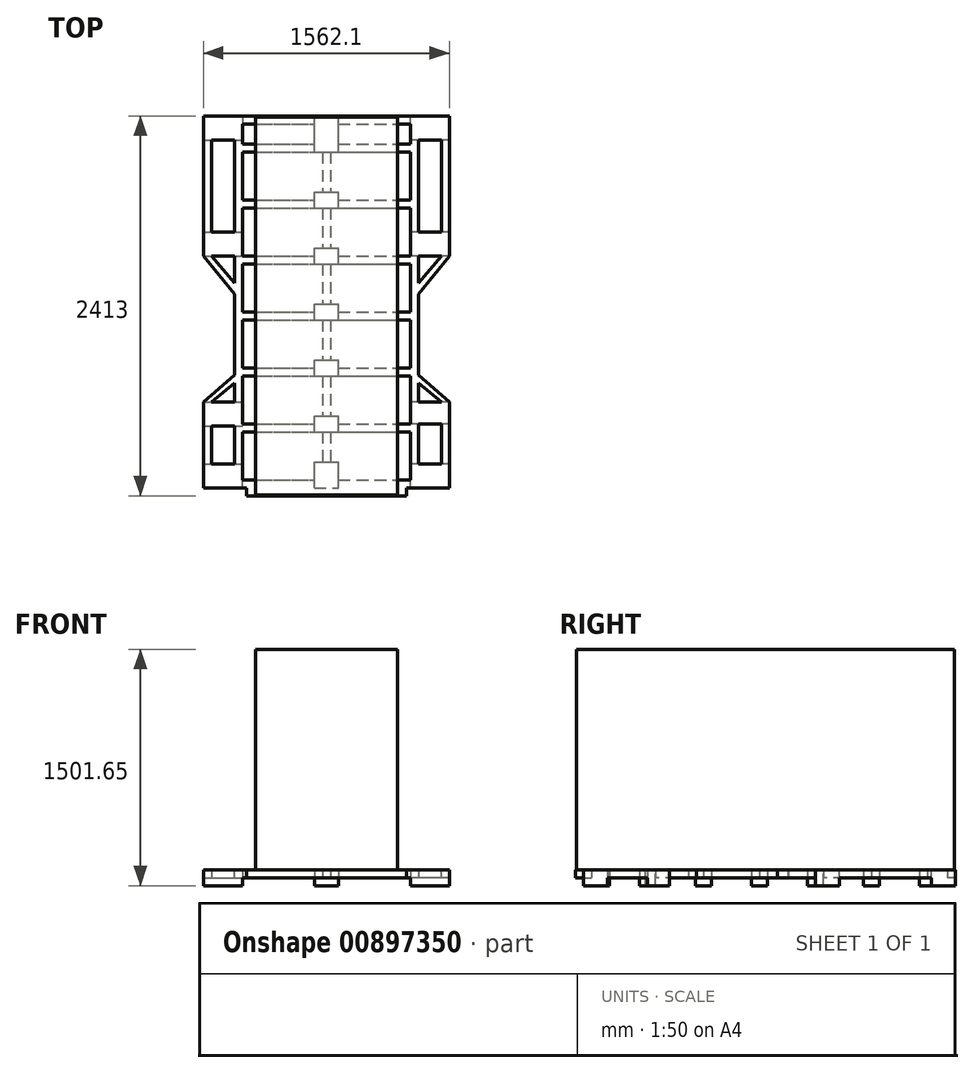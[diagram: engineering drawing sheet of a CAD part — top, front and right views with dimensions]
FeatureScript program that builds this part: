
annotation { "Feature Type Name" : "Feature", "Feature Type Description" : "" }
export const myFeature = defineFeature(function(context is Context, id is Id, definition is map)
    precondition{}
    {
        {
            var Q0;
            Q0=qCreatedBy(makeId("Top.planeOp"),FACE);
            var sketch = newSketch(context, id + "F0", { "sketchPlane" : qUnion([Q0])});
            skLineSegment(sketch, "E0.bottom", {"start": v(-826.89, 249) * mm, "end": v(341.51, 249) * mm});
            skLineSegment(sketch, "E0.top", {"start": v(-826.89, 299.8) * mm, "end": v(341.51, 299.8) * mm});
            skLineSegment(sketch, "E0.left", {"start": v(-826.89, 249) * mm, "end": v(-826.89, 299.8) * mm});
            skLineSegment(sketch, "E0.right", {"start": v(341.51, 249) * mm, "end": v(341.51, 299.8) * mm});
            skLineSegment(sketch, "E1.bottom", {"start": v(341.51, 299.8) * mm, "end": v(290.71, 299.8) * mm});
            skLineSegment(sketch, "E1.top", {"start": v(341.51, 2611.2) * mm, "end": v(290.71, 2611.2) * mm});
            skLineSegment(sketch, "E1.left", {"start": v(341.51, 299.8) * mm, "end": v(341.51, 2611.2) * mm});
            skLineSegment(sketch, "E1.right", {"start": v(290.71, 299.8) * mm, "end": v(290.71, 2611.2) * mm});
            skLineSegment(sketch, "E2.bottom", {"start": v(-826.89, 299.8) * mm, "end": v(-776.09, 299.8) * mm});
            skLineSegment(sketch, "E2.top", {"start": v(-826.89, 2611.2) * mm, "end": v(-776.09, 2611.2) * mm});
            skLineSegment(sketch, "E2.left", {"start": v(-826.89, 299.8) * mm, "end": v(-826.89, 2611.2) * mm});
            skLineSegment(sketch, "E2.right", {"start": v(-776.09, 299.8) * mm, "end": v(-776.09, 2611.2) * mm});
            skLineSegment(sketch, "E3.bottom", {"start": v(-826.89, 2611.2) * mm, "end": v(341.51, 2611.2) * mm});
            skLineSegment(sketch, "E3.top", {"start": v(-826.89, 2560.4) * mm, "end": v(341.51, 2560.4) * mm});
            skLineSegment(sketch, "E3.left", {"start": v(-826.89, 2611.2) * mm, "end": v(-826.89, 2560.4) * mm});
            skLineSegment(sketch, "E3.right", {"start": v(341.51, 2611.2) * mm, "end": v(341.51, 2560.4) * mm});
            skLineSegment(sketch, "E4.bottom", {"start": v(-826.89, 2611.2) * mm, "end": v(-1023.74, 2611.2) * mm});
            skLineSegment(sketch, "E4.top", {"start": v(-826.89, 2560.4) * mm, "end": v(-1023.74, 2560.4) * mm});
            skLineSegment(sketch, "E4.right", {"start": v(-1023.74, 2611.2) * mm, "end": v(-1023.74, 2560.4) * mm});
            skLineSegment(sketch, "E5.bottom", {"start": v(341.51, 2611.2) * mm, "end": v(538.36, 2611.2) * mm});
            skLineSegment(sketch, "E5.top", {"start": v(341.51, 2560.4) * mm, "end": v(538.36, 2560.4) * mm});
            skLineSegment(sketch, "E5.right", {"start": v(538.36, 2611.2) * mm, "end": v(538.36, 2560.4) * mm});
            skLineSegment(sketch, "E6.bottom", {"start": v(-1023.74, 2560.4) * mm, "end": v(-972.94, 2560.4) * mm});
            skLineSegment(sketch, "E6.top", {"start": v(-1023.74, 1722.2) * mm, "end": v(-972.94, 1722.2) * mm});
            skLineSegment(sketch, "E6.left", {"start": v(-1023.74, 2560.4) * mm, "end": v(-1023.74, 1722.2) * mm});
            skLineSegment(sketch, "E6.right", {"start": v(-972.94, 2560.4) * mm, "end": v(-972.94, 1722.2) * mm});
            skLineSegment(sketch, "E7.bottom", {"start": v(538.36, 2560.4) * mm, "end": v(487.56, 2560.4) * mm});
            skLineSegment(sketch, "E7.top", {"start": v(538.36, 1722.2) * mm, "end": v(487.56, 1722.2) * mm});
            skLineSegment(sketch, "E7.left", {"start": v(538.36, 2560.4) * mm, "end": v(538.36, 1722.2) * mm});
            skLineSegment(sketch, "E7.right", {"start": v(487.56, 2560.4) * mm, "end": v(487.56, 1722.2) * mm});
            skLineSegment(sketch, "E8", {"start": v(341.51, 2560.4) * mm, "end": v(341.51, 1480.9) * mm});
            skLineSegment(sketch, "E9", {"start": v(-826.89, 2560.4) * mm, "end": v(-826.89, 1480.9) * mm});
            skLineSegment(sketch, "E10", {"start": v(341.51, 1480.9) * mm, "end": v(538.36, 1722.2) * mm});
            skLineSegment(sketch, "E11", {"start": v(-1023.74, 1722.2) * mm, "end": v(-826.89, 1480.9) * mm});
            skLineSegment(sketch, "E12.bottom", {"start": v(341.51, 249) * mm, "end": v(538.36, 249) * mm});
            skLineSegment(sketch, "E12.top", {"start": v(341.51, 299.8) * mm, "end": v(538.36, 299.8) * mm});
            skLineSegment(sketch, "E12.right", {"start": v(538.36, 249) * mm, "end": v(538.36, 299.8) * mm});
            skLineSegment(sketch, "E13.bottom", {"start": v(-826.89, 249) * mm, "end": v(-1023.74, 249) * mm});
            skLineSegment(sketch, "E13.top", {"start": v(-826.89, 299.8) * mm, "end": v(-1023.74, 299.8) * mm});
            skLineSegment(sketch, "E13.right", {"start": v(-1023.74, 249) * mm, "end": v(-1023.74, 299.8) * mm});
            skLineSegment(sketch, "E14.bottom", {"start": v(-1023.74, 299.8) * mm, "end": v(-972.94, 299.8) * mm});
            skLineSegment(sketch, "E14.top", {"start": v(-1023.74, 795.1) * mm, "end": v(-972.94, 795.1) * mm});
            skLineSegment(sketch, "E14.left", {"start": v(-1023.74, 299.8) * mm, "end": v(-1023.74, 795.1) * mm});
            skLineSegment(sketch, "E14.right", {"start": v(-972.94, 299.8) * mm, "end": v(-972.94, 795.1) * mm});
            skLineSegment(sketch, "E15.bottom", {"start": v(538.36, 299.8) * mm, "end": v(487.56, 299.8) * mm});
            skLineSegment(sketch, "E15.top", {"start": v(538.36, 795.1) * mm, "end": v(487.56, 795.1) * mm});
            skLineSegment(sketch, "E15.left", {"start": v(538.36, 299.8) * mm, "end": v(538.36, 795.1) * mm});
            skLineSegment(sketch, "E15.right", {"start": v(487.56, 299.8) * mm, "end": v(487.56, 795.1) * mm});
            skLineSegment(sketch, "E16", {"start": v(-1023.74, 795.1) * mm, "end": v(-826.89, 966.54) * mm});
            skLineSegment(sketch, "E17", {"start": v(538.36, 795.1) * mm, "end": v(341.51, 966.54) * mm});
            skLineSegment(sketch, "E18.bottom", {"start": v(-776.09, 604.6) * mm, "end": v(290.71, 604.6) * mm});
            skLineSegment(sketch, "E18.top", {"start": v(-776.09, 655.4) * mm, "end": v(290.71, 655.4) * mm});
            skLineSegment(sketch, "E18.left", {"start": v(-776.09, 604.6) * mm, "end": v(-776.09, 655.4) * mm});
            skLineSegment(sketch, "E18.right", {"start": v(290.71, 604.6) * mm, "end": v(290.71, 655.4) * mm});
            skLineSegment(sketch, "E19.bottom", {"start": v(-776.09, 1011) * mm, "end": v(290.71, 1011) * mm});
            skLineSegment(sketch, "E19.top", {"start": v(-776.09, 960.2) * mm, "end": v(290.71, 960.2) * mm});
            skLineSegment(sketch, "E19.left", {"start": v(-776.09, 1011) * mm, "end": v(-776.09, 960.2) * mm});
            skLineSegment(sketch, "E19.right", {"start": v(290.71, 1011) * mm, "end": v(290.71, 960.2) * mm});
            skLineSegment(sketch, "E20.bottom", {"start": v(-776.09, 1366.6) * mm, "end": v(290.71, 1366.6) * mm});
            skLineSegment(sketch, "E20.top", {"start": v(-776.09, 1315.8) * mm, "end": v(290.71, 1315.8) * mm});
            skLineSegment(sketch, "E20.left", {"start": v(-776.09, 1366.6) * mm, "end": v(-776.09, 1315.8) * mm});
            skLineSegment(sketch, "E20.right", {"start": v(290.71, 1366.6) * mm, "end": v(290.71, 1315.8) * mm});
            skLineSegment(sketch, "E21.bottom", {"start": v(-776.09, 1722.2) * mm, "end": v(290.71, 1722.2) * mm});
            skLineSegment(sketch, "E21.top", {"start": v(-776.09, 1671.4) * mm, "end": v(290.71, 1671.4) * mm});
            skLineSegment(sketch, "E21.left", {"start": v(-776.09, 1722.2) * mm, "end": v(-776.09, 1671.4) * mm});
            skLineSegment(sketch, "E21.right", {"start": v(290.71, 1722.2) * mm, "end": v(290.71, 1671.4) * mm});
            skLineSegment(sketch, "E22.bottom", {"start": v(-776.09, 2077.8) * mm, "end": v(290.71, 2077.8) * mm});
            skLineSegment(sketch, "E22.top", {"start": v(-776.09, 2027) * mm, "end": v(290.71, 2027) * mm});
            skLineSegment(sketch, "E22.left", {"start": v(-776.09, 2077.8) * mm, "end": v(-776.09, 2027) * mm});
            skLineSegment(sketch, "E22.right", {"start": v(290.71, 2077.8) * mm, "end": v(290.71, 2027) * mm});
            skLineSegment(sketch, "E23.bottom", {"start": v(-776.09, 2433.4) * mm, "end": v(290.71, 2433.4) * mm});
            skLineSegment(sketch, "E23.top", {"start": v(-776.09, 2382.6) * mm, "end": v(290.71, 2382.6) * mm});
            skLineSegment(sketch, "E23.left", {"start": v(-776.09, 2433.4) * mm, "end": v(-776.09, 2382.6) * mm});
            skLineSegment(sketch, "E23.right", {"start": v(290.71, 2433.4) * mm, "end": v(290.71, 2382.6) * mm});
            skLineSegment(sketch, "E24.bottom", {"start": v(-268.09, 2560.4) * mm, "end": v(-217.29, 2560.4) * mm});
            skLineSegment(sketch, "E24.top", {"start": v(-268.09, 2433.4) * mm, "end": v(-217.29, 2433.4) * mm});
            skLineSegment(sketch, "E24.left", {"start": v(-268.09, 2560.4) * mm, "end": v(-268.09, 2433.4) * mm});
            skLineSegment(sketch, "E24.right", {"start": v(-217.29, 2560.4) * mm, "end": v(-217.29, 2433.4) * mm});
            skLineSegment(sketch, "E25.bottom", {"start": v(-268.09, 2382.6) * mm, "end": v(-217.29, 2382.6) * mm});
            skLineSegment(sketch, "E25.top", {"start": v(-268.09, 2077.8) * mm, "end": v(-217.29, 2077.8) * mm});
            skLineSegment(sketch, "E25.left", {"start": v(-268.09, 2382.6) * mm, "end": v(-268.09, 2077.8) * mm});
            skLineSegment(sketch, "E25.right", {"start": v(-217.29, 2382.6) * mm, "end": v(-217.29, 2077.8) * mm});
            skLineSegment(sketch, "E26.bottom", {"start": v(-268.09, 2027) * mm, "end": v(-217.29, 2027) * mm});
            skLineSegment(sketch, "E26.top", {"start": v(-268.09, 1722.2) * mm, "end": v(-217.29, 1722.2) * mm});
            skLineSegment(sketch, "E26.left", {"start": v(-268.09, 2027) * mm, "end": v(-268.09, 1722.2) * mm});
            skLineSegment(sketch, "E26.right", {"start": v(-217.29, 2027) * mm, "end": v(-217.29, 1722.2) * mm});
            skLineSegment(sketch, "E27.bottom", {"start": v(-268.09, 1671.4) * mm, "end": v(-217.29, 1671.4) * mm});
            skLineSegment(sketch, "E27.top", {"start": v(-268.09, 1366.6) * mm, "end": v(-217.29, 1366.6) * mm});
            skLineSegment(sketch, "E27.left", {"start": v(-268.09, 1671.4) * mm, "end": v(-268.09, 1366.6) * mm});
            skLineSegment(sketch, "E27.right", {"start": v(-217.29, 1671.4) * mm, "end": v(-217.29, 1366.6) * mm});
            skLineSegment(sketch, "E28.bottom", {"start": v(-268.09, 1315.8) * mm, "end": v(-217.29, 1315.8) * mm});
            skLineSegment(sketch, "E28.top", {"start": v(-268.09, 1011) * mm, "end": v(-217.29, 1011) * mm});
            skLineSegment(sketch, "E28.left", {"start": v(-268.09, 1315.8) * mm, "end": v(-268.09, 1011) * mm});
            skLineSegment(sketch, "E28.right", {"start": v(-217.29, 1315.8) * mm, "end": v(-217.29, 1011) * mm});
            skLineSegment(sketch, "E29.bottom", {"start": v(-268.09, 960.2) * mm, "end": v(-217.29, 960.2) * mm});
            skLineSegment(sketch, "E29.top", {"start": v(-268.09, 655.4) * mm, "end": v(-217.29, 655.4) * mm});
            skLineSegment(sketch, "E29.left", {"start": v(-268.09, 960.2) * mm, "end": v(-268.09, 655.4) * mm});
            skLineSegment(sketch, "E29.right", {"start": v(-217.29, 960.2) * mm, "end": v(-217.29, 655.4) * mm});
            skLineSegment(sketch, "E30.bottom", {"start": v(-268.09, 604.6) * mm, "end": v(-217.29, 604.6) * mm});
            skLineSegment(sketch, "E30.top", {"start": v(-268.09, 299.8) * mm, "end": v(-217.29, 299.8) * mm});
            skLineSegment(sketch, "E30.left", {"start": v(-268.09, 604.6) * mm, "end": v(-268.09, 299.8) * mm});
            skLineSegment(sketch, "E30.right", {"start": v(-217.29, 604.6) * mm, "end": v(-217.29, 299.8) * mm});
            skLineSegment(sketch, "E31", {"start": v(487.56, 795.1) * mm, "end": v(341.51, 915.74) * mm});
            skLineSegment(sketch, "E32", {"start": v(-972.94, 795.1) * mm, "end": v(-826.89, 915.74) * mm});
            skLineSegment(sketch, "E33", {"start": v(-972.94, 1722.2) * mm, "end": v(-826.89, 1550.62) * mm});
            skLineSegment(sketch, "E34", {"start": v(487.56, 1722.2) * mm, "end": v(341.51, 1547.67) * mm});
            skSolve(sketch);
        }
        {
            var Q0;
            {var subQ5=sQuery(id+"F0.wireOp",EDGE,"E4.bottom");Q0=makeQuery(id+"F0.imprint","IMPRINT",FACE,{"disambiguationData":[TD([[makeQuery(id+"F0.imprint","IMPRINT",EDGE,{"derivedFrom":subQ5}),1.0]])]});}
            var Q1;
            {var subQ4=sQuery(id+"F0.wireOp",EDGE,"E3.bottom");Q1=makeQuery(id+"F0.imprint","IMPRINT",FACE,{"disambiguationData":[TD([[makeQuery(id+"F0.imprint","IMPRINT",EDGE,{"derivedFrom":subQ4}),-1.0]])]});}
            var Q2;
            {var subQ0=sQuery(id+"F0.wireOp",EDGE,"E2.top");Q2=makeQuery(id+"F0.imprint","IMPRINT",FACE,{"disambiguationData":[TD([[makeQuery(id+"F0.imprint","IMPRINT",EDGE,{"derivedFrom":subQ0}),-1.0]])]});}
            var Q3;
            {var subQ7=sQuery(id+"F0.wireOp",EDGE,"E2.left");var subQ11=makeQuery(id+"F0.imprint","INTERSECT",VERTEX,{"derivedFrom":[subQ7,sQuery(id+"F0.wireOp",EDGE,"E11")]});Q3=makeQuery(id+"F0.imprint","IMPRINT",FACE,{"disambiguationData":[TD([[makeQuery(id+"F0.imprint","IMPRINT",EDGE,{"disambiguationData":[TD([[subQ11,1.0]])],"derivedFrom":subQ7}),-1.0]])]});}
            var Q4;
            {var subQ5=sQuery(id+"F0.wireOp",EDGE,"E5.bottom");Q4=makeQuery(id+"F0.imprint","IMPRINT",FACE,{"disambiguationData":[TD([[makeQuery(id+"F0.imprint","IMPRINT",EDGE,{"derivedFrom":subQ5}),-1.0]])]});}
            var Q5;
            {var subQ0=sQuery(id+"F0.wireOp",EDGE,"E1.top");Q5=makeQuery(id+"F0.imprint","IMPRINT",FACE,{"disambiguationData":[TD([[makeQuery(id+"F0.imprint","IMPRINT",EDGE,{"derivedFrom":subQ0}),1.0]])]});}
            var Q6;
            {var subQ7=sQuery(id+"F0.wireOp",EDGE,"E1.left");var subQ8=makeQuery(id+"F0.imprint","INTERSECT",VERTEX,{"derivedFrom":[subQ7,sQuery(id+"F0.wireOp",EDGE,"E17")]});Q6=makeQuery(id+"F0.imprint","IMPRINT",FACE,{"disambiguationData":[TD([[makeQuery(id+"F0.imprint","IMPRINT",EDGE,{"disambiguationData":[TD([[subQ8,-1.0]])],"derivedFrom":subQ7}),1.0]])]});}
            var Q7;
            {var subQ5=sQuery(id+"F0.wireOp",EDGE,"E1.right");var subQ7=sQuery(id+"F0.wireOp",EDGE,"E23.top");var subQ9=makeQuery(id+"F0.imprint","INTERSECT",VERTEX,{"derivedFrom":[subQ5,subQ7]});Q7=makeQuery(id+"F0.imprint","IMPRINT",FACE,{"disambiguationData":[TD([[makeQuery(id+"F0.imprint","IMPRINT",EDGE,{"disambiguationData":[TD([[subQ9,-1.0]])],"derivedFrom":subQ5}),1.0]])]});}
            var Q8;
            {var subQ2=sQuery(id+"F0.wireOp",EDGE,"E24.left");Q8=makeQuery(id+"F0.imprint","IMPRINT",FACE,{"disambiguationData":[TD([[makeQuery(id+"F0.imprint","IMPRINT",EDGE,{"derivedFrom":subQ2}),1.0]])]});}
            var Q9;
            {var subQ2=sQuery(id+"F0.wireOp",EDGE,"E25.left");Q9=makeQuery(id+"F0.imprint","IMPRINT",FACE,{"disambiguationData":[TD([[makeQuery(id+"F0.imprint","IMPRINT",EDGE,{"derivedFrom":subQ2}),1.0]])]});}
            var Q10;
            {var subQ0=sQuery(id+"F0.wireOp",EDGE,"E22.bottom");var subQ7=sQuery(id+"F0.wireOp",EDGE,"E1.right");var subQ8=makeQuery(id+"F0.imprint","INTERSECT",VERTEX,{"derivedFrom":[subQ7,subQ0]});Q10=makeQuery(id+"F0.imprint","IMPRINT",FACE,{"disambiguationData":[TD([[makeQuery(id+"F0.imprint","IMPRINT",EDGE,{"disambiguationData":[TD([[subQ8,1.0]])],"derivedFrom":subQ7}),1.0]])]});}
            var Q11;
            {var subQ2=sQuery(id+"F0.wireOp",EDGE,"E26.left");Q11=makeQuery(id+"F0.imprint","IMPRINT",FACE,{"disambiguationData":[TD([[makeQuery(id+"F0.imprint","IMPRINT",EDGE,{"derivedFrom":subQ2}),1.0]])]});}
            var Q12;
            Q12=makeQuery(id+"F0.imprint","IMPRINT",FACE,{"disambiguationData":[TD([[makeQuery(id+"F0.imprint","IMPRINT",EDGE,{"derivedFrom":sQuery(id+"F0.wireOp",EDGE,"E7.top")}),-1.0]])]});
            var Q13;
            Q13=makeQuery(id+"F0.imprint","IMPRINT",FACE,{"disambiguationData":[TD([[makeQuery(id+"F0.imprint","IMPRINT",EDGE,{"derivedFrom":sQuery(id+"F0.wireOp",EDGE,"E7.top")}),1.0]])]});
            var Q14;
            {var subQ0=sQuery(id+"F0.wireOp",EDGE,"E21.bottom");var subQ5=sQuery(id+"F0.wireOp",EDGE,"E1.right");var subQ6=makeQuery(id+"F0.imprint","INTERSECT",VERTEX,{"derivedFrom":[subQ5,subQ0]});Q14=makeQuery(id+"F0.imprint","IMPRINT",FACE,{"disambiguationData":[TD([[makeQuery(id+"F0.imprint","IMPRINT",EDGE,{"disambiguationData":[TD([[subQ6,1.0]])],"derivedFrom":subQ5}),1.0]])]});}
            var Q15;
            Q15=makeQuery(id+"F0.imprint","IMPRINT",FACE,{"disambiguationData":[TD([[makeQuery(id+"F0.imprint","IMPRINT",EDGE,{"derivedFrom":sQuery(id+"F0.wireOp",EDGE,"E6.top")}),1.0]])]});
            var Q16;
            Q16=makeQuery(id+"F0.imprint","IMPRINT",FACE,{"disambiguationData":[TD([[makeQuery(id+"F0.imprint","IMPRINT",EDGE,{"derivedFrom":sQuery(id+"F0.wireOp",EDGE,"E6.top")}),-1.0]])]});
            var Q17;
            {var subQ4=sQuery(id+"F0.wireOp",EDGE,"E20.top");var subQ5=sQuery(id+"F0.wireOp",EDGE,"E1.right");var subQ6=makeQuery(id+"F0.imprint","INTERSECT",VERTEX,{"derivedFrom":[subQ5,subQ4]});Q17=makeQuery(id+"F0.imprint","IMPRINT",FACE,{"disambiguationData":[TD([[makeQuery(id+"F0.imprint","IMPRINT",EDGE,{"disambiguationData":[TD([[subQ6,-1.0]])],"derivedFrom":subQ5}),1.0]])]});}
            var Q18;
            {var subQ2=sQuery(id+"F0.wireOp",EDGE,"E27.left");Q18=makeQuery(id+"F0.imprint","IMPRINT",FACE,{"disambiguationData":[TD([[makeQuery(id+"F0.imprint","IMPRINT",EDGE,{"derivedFrom":subQ2}),1.0]])]});}
            var Q19;
            {var subQ2=sQuery(id+"F0.wireOp",EDGE,"E28.left");Q19=makeQuery(id+"F0.imprint","IMPRINT",FACE,{"disambiguationData":[TD([[makeQuery(id+"F0.imprint","IMPRINT",EDGE,{"derivedFrom":subQ2}),1.0]])]});}
            var Q20;
            {var subQ0=sQuery(id+"F0.wireOp",EDGE,"E19.bottom");var subQ2=sQuery(id+"F0.wireOp",EDGE,"E1.right");var subQ3=makeQuery(id+"F0.imprint","INTERSECT",VERTEX,{"derivedFrom":[subQ2,subQ0]});Q20=makeQuery(id+"F0.imprint","IMPRINT",FACE,{"disambiguationData":[TD([[makeQuery(id+"F0.imprint","IMPRINT",EDGE,{"disambiguationData":[TD([[subQ3,1.0]])],"derivedFrom":subQ2}),1.0]])]});}
            var Q21;
            {var subQ2=sQuery(id+"F0.wireOp",EDGE,"E29.left");Q21=makeQuery(id+"F0.imprint","IMPRINT",FACE,{"disambiguationData":[TD([[makeQuery(id+"F0.imprint","IMPRINT",EDGE,{"derivedFrom":subQ2}),1.0]])]});}
            var Q22;
            {var subQ5=sQuery(id+"F0.wireOp",EDGE,"E1.right");var subQ7=sQuery(id+"F0.wireOp",EDGE,"E18.top");var subQ10=makeQuery(id+"F0.imprint","INTERSECT",VERTEX,{"derivedFrom":[subQ5,subQ7]});Q22=makeQuery(id+"F0.imprint","IMPRINT",FACE,{"disambiguationData":[TD([[makeQuery(id+"F0.imprint","IMPRINT",EDGE,{"disambiguationData":[TD([[subQ10,1.0]])],"derivedFrom":subQ5}),1.0]])]});}
            var Q23;
            {var subQ2=sQuery(id+"F0.wireOp",EDGE,"E30.left");Q23=makeQuery(id+"F0.imprint","IMPRINT",FACE,{"disambiguationData":[TD([[makeQuery(id+"F0.imprint","IMPRINT",EDGE,{"derivedFrom":subQ2}),1.0]])]});}
            var Q24;
            Q24=makeQuery(id+"F0.imprint","IMPRINT",FACE,{"disambiguationData":[TD([[makeQuery(id+"F0.imprint","IMPRINT",EDGE,{"derivedFrom":sQuery(id+"F0.wireOp",EDGE,"E0.bottom")}),1.0]])]});
            var Q25;
            {var subQ3=sQuery(id+"F0.wireOp",EDGE,"E0.right");Q25=makeQuery(id+"F0.imprint","IMPRINT",FACE,{"disambiguationData":[TD([[makeQuery(id+"F0.imprint","IMPRINT",EDGE,{"derivedFrom":subQ3}),-1.0]])]});}
            var Q26;
            Q26=makeQuery(id+"F0.imprint","IMPRINT",FACE,{"disambiguationData":[TD([[makeQuery(id+"F0.imprint","IMPRINT",EDGE,{"derivedFrom":sQuery(id+"F0.wireOp",EDGE,"E15.top")}),1.0]])]});
            var Q27;
            Q27=makeQuery(id+"F0.imprint","IMPRINT",FACE,{"disambiguationData":[TD([[makeQuery(id+"F0.imprint","IMPRINT",EDGE,{"derivedFrom":sQuery(id+"F0.wireOp",EDGE,"E15.top")}),-1.0]])]});
            var Q28;
            Q28=makeQuery(id+"F0.imprint","IMPRINT",FACE,{"disambiguationData":[TD([[makeQuery(id+"F0.imprint","IMPRINT",EDGE,{"derivedFrom":sQuery(id+"F0.wireOp",EDGE,"E14.top")}),1.0]])]});
            var Q29;
            Q29=makeQuery(id+"F0.imprint","IMPRINT",FACE,{"disambiguationData":[TD([[makeQuery(id+"F0.imprint","IMPRINT",EDGE,{"derivedFrom":sQuery(id+"F0.wireOp",EDGE,"E14.top")}),-1.0]])]});
            var Q30;
            {var subQ3=sQuery(id+"F0.wireOp",EDGE,"E0.left");Q30=makeQuery(id+"F0.imprint","IMPRINT",FACE,{"disambiguationData":[TD([[makeQuery(id+"F0.imprint","IMPRINT",EDGE,{"derivedFrom":subQ3}),1.0]])]});}
            extrude(context, id + "F1", {"entities" : qUnion([Q0, Q1, Q2, Q3, Q4, Q5, Q6, Q7, Q8, Q9, Q10, Q11, Q12, Q13, Q14, Q15, Q16, Q17, Q18, Q19, Q20, Q21, Q22, Q23, Q24, Q25, Q26, Q27, Q28, Q29, Q30]), "endBound" : BoundingType.SYMMETRIC, "depth" : 50.8 * mm, "offsetDistance" : 25.4 * mm});
        }
        {
            var Q0;
            Q0=makeQuery(id+"F1.opExtrude","CAP_FACE",FACE,{"disambiguationData":[OSD([sQuery(id+"F0.wireOp",EDGE,"E0.bottom"),sQuery(id+"F0.wireOp",EDGE,"E0.top"),sQuery(id+"F0.wireOp",EDGE,"E1.top"),sQuery(id+"F0.wireOp",EDGE,"E1.left"),sQuery(id+"F0.wireOp",EDGE,"E1.right"),sQuery(id+"F0.wireOp",EDGE,"E2.top"),sQuery(id+"F0.wireOp",EDGE,"E2.left"),sQuery(id+"F0.wireOp",EDGE,"E2.right"),sQuery(id+"F0.wireOp",EDGE,"E3.bottom"),sQuery(id+"F0.wireOp",EDGE,"E3.top"),sQuery(id+"F0.wireOp",EDGE,"E4.bottom"),sQuery(id+"F0.wireOp",EDGE,"E4.top"),sQuery(id+"F0.wireOp",EDGE,"E4.right"),sQuery(id+"F0.wireOp",EDGE,"E5.bottom"),sQuery(id+"F0.wireOp",EDGE,"E5.top"),sQuery(id+"F0.wireOp",EDGE,"E5.right"),sQuery(id+"F0.wireOp",EDGE,"E6.left"),sQuery(id+"F0.wireOp",EDGE,"E6.right"),sQuery(id+"F0.wireOp",EDGE,"E7.left"),sQuery(id+"F0.wireOp",EDGE,"E7.right"),sQuery(id+"F0.wireOp",EDGE,"E10"),sQuery(id+"F0.wireOp",EDGE,"E11"),sQuery(id+"F0.wireOp",EDGE,"E12.bottom"),sQuery(id+"F0.wireOp",EDGE,"E12.top"),sQuery(id+"F0.wireOp",EDGE,"E12.right"),sQuery(id+"F0.wireOp",EDGE,"E13.bottom"),sQuery(id+"F0.wireOp",EDGE,"E13.top"),sQuery(id+"F0.wireOp",EDGE,"E13.right"),sQuery(id+"F0.wireOp",EDGE,"E14.left"),sQuery(id+"F0.wireOp",EDGE,"E14.right"),sQuery(id+"F0.wireOp",EDGE,"E15.left"),sQuery(id+"F0.wireOp",EDGE,"E15.right"),sQuery(id+"F0.wireOp",EDGE,"E16"),sQuery(id+"F0.wireOp",EDGE,"E17"),sQuery(id+"F0.wireOp",EDGE,"E18.bottom"),sQuery(id+"F0.wireOp",EDGE,"E18.top"),sQuery(id+"F0.wireOp",EDGE,"E19.bottom"),sQuery(id+"F0.wireOp",EDGE,"E19.top"),sQuery(id+"F0.wireOp",EDGE,"E20.bottom"),sQuery(id+"F0.wireOp",EDGE,"E20.top"),sQuery(id+"F0.wireOp",EDGE,"E21.bottom"),sQuery(id+"F0.wireOp",EDGE,"E21.top"),sQuery(id+"F0.wireOp",EDGE,"E22.bottom"),sQuery(id+"F0.wireOp",EDGE,"E22.top"),sQuery(id+"F0.wireOp",EDGE,"E23.bottom"),sQuery(id+"F0.wireOp",EDGE,"E23.top"),sQuery(id+"F0.wireOp",EDGE,"E24.left"),sQuery(id+"F0.wireOp",EDGE,"E24.right"),sQuery(id+"F0.wireOp",EDGE,"E25.left"),sQuery(id+"F0.wireOp",EDGE,"E25.right"),sQuery(id+"F0.wireOp",EDGE,"E26.left"),sQuery(id+"F0.wireOp",EDGE,"E26.right"),sQuery(id+"F0.wireOp",EDGE,"E27.left"),sQuery(id+"F0.wireOp",EDGE,"E27.right"),sQuery(id+"F0.wireOp",EDGE,"E28.left"),sQuery(id+"F0.wireOp",EDGE,"E28.right"),sQuery(id+"F0.wireOp",EDGE,"E29.left"),sQuery(id+"F0.wireOp",EDGE,"E29.right"),sQuery(id+"F0.wireOp",EDGE,"E30.left"),sQuery(id+"F0.wireOp",EDGE,"E30.right"),sQuery(id+"F0.wireOp",EDGE,"E31"),sQuery(id+"F0.wireOp",EDGE,"E32"),sQuery(id+"F0.wireOp",EDGE,"E33"),sQuery(id+"F0.wireOp",EDGE,"E34")])],"isStart":true});
            var sketch = newSketch(context, id + "F2", { "sketchPlane" : qUnion([Q0])});
            skLineSegment(sketch, "E35.bottom", {"start": v(-1023.74, -249) * mm, "end": v(-776.09, -249) * mm});
            skLineSegment(sketch, "E35.top", {"start": v(-1023.74, -401.4) * mm, "end": v(-776.09, -401.4) * mm});
            skLineSegment(sketch, "E35.left", {"start": v(-1023.74, -249) * mm, "end": v(-1023.74, -401.4) * mm});
            skLineSegment(sketch, "E35.right", {"start": v(-776.09, -249) * mm, "end": v(-776.09, -401.4) * mm});
            skLineSegment(sketch, "E36.bottom", {"start": v(538.36, -249) * mm, "end": v(290.71, -249) * mm});
            skLineSegment(sketch, "E36.top", {"start": v(538.36, -401.4) * mm, "end": v(290.71, -401.4) * mm});
            skLineSegment(sketch, "E36.left", {"start": v(538.36, -249) * mm, "end": v(538.36, -401.4) * mm});
            skLineSegment(sketch, "E36.right", {"start": v(290.71, -249) * mm, "end": v(290.71, -401.4) * mm});
            skLineSegment(sketch, "E37.bottom", {"start": v(-318.89, -249) * mm, "end": v(-166.49, -249) * mm});
            skLineSegment(sketch, "E37.top", {"start": v(-318.89, -414.1) * mm, "end": v(-166.49, -414.1) * mm});
            skLineSegment(sketch, "E37.left", {"start": v(-318.89, -249) * mm, "end": v(-318.89, -414.1) * mm});
            skLineSegment(sketch, "E37.right", {"start": v(-166.49, -249) * mm, "end": v(-166.49, -414.1) * mm});
            skLineSegment(sketch, "E38.bottom", {"start": v(-318.89, -960.2) * mm, "end": v(-166.49, -960.2) * mm});
            skLineSegment(sketch, "E38.top", {"start": v(-318.89, -1061.8) * mm, "end": v(-166.49, -1061.8) * mm});
            skLineSegment(sketch, "E38.left", {"start": v(-318.89, -960.2) * mm, "end": v(-318.89, -1061.8) * mm});
            skLineSegment(sketch, "E38.right", {"start": v(-166.49, -960.2) * mm, "end": v(-166.49, -1061.8) * mm});
            skLineSegment(sketch, "E39.bottom", {"start": v(-318.89, -604.6) * mm, "end": v(-166.49, -604.6) * mm});
            skLineSegment(sketch, "E39.top", {"start": v(-318.89, -706.2) * mm, "end": v(-166.49, -706.2) * mm});
            skLineSegment(sketch, "E39.left", {"start": v(-318.89, -604.6) * mm, "end": v(-318.89, -706.2) * mm});
            skLineSegment(sketch, "E39.right", {"start": v(-166.49, -604.6) * mm, "end": v(-166.49, -706.2) * mm});
            skLineSegment(sketch, "E40.bottom", {"start": v(-318.89, -1315.8) * mm, "end": v(-166.49, -1315.8) * mm});
            skLineSegment(sketch, "E40.top", {"start": v(-318.89, -1417.4) * mm, "end": v(-166.49, -1417.4) * mm});
            skLineSegment(sketch, "E40.left", {"start": v(-318.89, -1315.8) * mm, "end": v(-318.89, -1417.4) * mm});
            skLineSegment(sketch, "E40.right", {"start": v(-166.49, -1315.8) * mm, "end": v(-166.49, -1417.4) * mm});
            skLineSegment(sketch, "E41.bottom", {"start": v(-318.89, -1671.4) * mm, "end": v(-166.49, -1671.4) * mm});
            skLineSegment(sketch, "E41.top", {"start": v(-318.89, -1773) * mm, "end": v(-166.49, -1773) * mm});
            skLineSegment(sketch, "E41.left", {"start": v(-318.89, -1671.4) * mm, "end": v(-318.89, -1773) * mm});
            skLineSegment(sketch, "E41.right", {"start": v(-166.49, -1671.4) * mm, "end": v(-166.49, -1773) * mm});
            skLineSegment(sketch, "E42.bottom", {"start": v(-318.89, -2027) * mm, "end": v(-166.49, -2027) * mm});
            skLineSegment(sketch, "E42.top", {"start": v(-318.89, -2128.6) * mm, "end": v(-166.49, -2128.6) * mm});
            skLineSegment(sketch, "E42.left", {"start": v(-318.89, -2027) * mm, "end": v(-318.89, -2128.6) * mm});
            skLineSegment(sketch, "E42.right", {"start": v(-166.49, -2027) * mm, "end": v(-166.49, -2128.6) * mm});
            skLineSegment(sketch, "E43.bottom", {"start": v(-318.89, -2382.6) * mm, "end": v(-166.49, -2382.6) * mm});
            skLineSegment(sketch, "E43.top", {"start": v(-318.89, -2611.2) * mm, "end": v(-166.49, -2611.2) * mm});
            skLineSegment(sketch, "E43.left", {"start": v(-318.89, -2382.6) * mm, "end": v(-318.89, -2611.2) * mm});
            skLineSegment(sketch, "E43.right", {"start": v(-166.49, -2382.6) * mm, "end": v(-166.49, -2611.2) * mm});
            skLineSegment(sketch, "E44.bottom", {"start": v(-1023.74, -1722.2) * mm, "end": v(-776.09, -1722.2) * mm});
            skLineSegment(sketch, "E44.top", {"start": v(-1023.74, -1874.6) * mm, "end": v(-776.09, -1874.6) * mm});
            skLineSegment(sketch, "E44.left", {"start": v(-1023.74, -1722.2) * mm, "end": v(-1023.74, -1874.6) * mm});
            skLineSegment(sketch, "E44.right", {"start": v(-776.09, -1722.2) * mm, "end": v(-776.09, -1874.6) * mm});
            skLineSegment(sketch, "E45.bottom", {"start": v(538.36, -1722.2) * mm, "end": v(290.71, -1722.2) * mm});
            skLineSegment(sketch, "E45.top", {"start": v(538.36, -1874.6) * mm, "end": v(290.71, -1874.6) * mm});
            skLineSegment(sketch, "E45.left", {"start": v(538.36, -1722.2) * mm, "end": v(538.36, -1874.6) * mm});
            skLineSegment(sketch, "E45.right", {"start": v(290.71, -1722.2) * mm, "end": v(290.71, -1874.6) * mm});
            skLineSegment(sketch, "E46.bottom", {"start": v(538.36, -795.1) * mm, "end": v(290.71, -795.1) * mm});
            skLineSegment(sketch, "E46.top", {"start": v(538.36, -655.4) * mm, "end": v(290.71, -655.4) * mm});
            skLineSegment(sketch, "E46.left", {"start": v(538.36, -795.1) * mm, "end": v(538.36, -655.4) * mm});
            skLineSegment(sketch, "E46.right", {"start": v(290.71, -795.1) * mm, "end": v(290.71, -655.4) * mm});
            skLineSegment(sketch, "E47.bottom", {"start": v(-1023.74, -795.1) * mm, "end": v(-776.09, -795.1) * mm});
            skLineSegment(sketch, "E47.top", {"start": v(-1023.74, -642.7) * mm, "end": v(-776.09, -642.7) * mm});
            skLineSegment(sketch, "E47.left", {"start": v(-1023.74, -795.1) * mm, "end": v(-1023.74, -642.7) * mm});
            skLineSegment(sketch, "E47.right", {"start": v(-776.09, -795.1) * mm, "end": v(-776.09, -642.7) * mm});
            skLineSegment(sketch, "E48.bottom", {"start": v(538.36, -2611.2) * mm, "end": v(290.71, -2611.2) * mm});
            skLineSegment(sketch, "E48.top", {"start": v(538.36, -2458.8) * mm, "end": v(290.71, -2458.8) * mm});
            skLineSegment(sketch, "E48.left", {"start": v(538.36, -2611.2) * mm, "end": v(538.36, -2458.8) * mm});
            skLineSegment(sketch, "E48.right", {"start": v(290.71, -2611.2) * mm, "end": v(290.71, -2458.8) * mm});
            skLineSegment(sketch, "E49.bottom", {"start": v(-1023.74, -2611.2) * mm, "end": v(-776.09, -2611.2) * mm});
            skLineSegment(sketch, "E49.top", {"start": v(-1023.74, -2458.8) * mm, "end": v(-776.09, -2458.8) * mm});
            skLineSegment(sketch, "E49.left", {"start": v(-1023.74, -2611.2) * mm, "end": v(-1023.74, -2458.8) * mm});
            skLineSegment(sketch, "E49.right", {"start": v(-776.09, -2611.2) * mm, "end": v(-776.09, -2458.8) * mm});
            skSolve(sketch);
        }
        {
            var Q0;
            {var subQ3=sQuery(id+"F0.wireOp",EDGE,"E13.top");var subQ7=makeQuery(id+"F1.opExtrude","CAP_EDGE",EDGE,{"disambiguationData":[OSD([subQ3])],"isStart":true});Q0=makeQuery(id+"F2.imprint","IMPRINT",FACE,{"disambiguationData":[TD([[makeQuery(id+"F2.imprint","IMPRINT",EDGE,{"derivedFrom":subQ7}),1.0]])]});}
            var Q1;
            {var subQ15=sQuery(id+"F2.wireOp",EDGE,"E35.bottom");Q1=makeQuery(id+"F2.imprint","IMPRINT",FACE,{"disambiguationData":[TD([[makeQuery(id+"F2.imprint","IMPRINT",EDGE,{"derivedFrom":subQ15}),-1.0]])]});}
            var Q2;
            {var subQ1=sQuery(id+"F2.wireOp",EDGE,"E37.bottom");Q2=makeQuery(id+"F2.imprint","IMPRINT",FACE,{"disambiguationData":[TD([[makeQuery(id+"F2.imprint","IMPRINT",EDGE,{"derivedFrom":subQ1}),-1.0]])]});}
            var Q3;
            {var subQ0=sQuery(id+"F2.wireOp",EDGE,"E37.left");var subQ1=sQuery(id+"F2.wireOp",EDGE,"E37.top");var subQ2=makeQuery(id+"F2.imprint","INTERSECT",VERTEX,{"derivedFrom":[subQ1,subQ0]});Q3=makeQuery(id+"F2.imprint","IMPRINT",FACE,{"disambiguationData":[TD([[makeQuery(id+"F2.imprint","IMPRINT",EDGE,{"disambiguationData":[TD([[subQ2,-1.0]])],"derivedFrom":subQ1}),1.0]])]});}
            var Q4;
            {var subQ0=sQuery(id+"F2.wireOp",EDGE,"E37.right");var subQ1=sQuery(id+"F2.wireOp",EDGE,"E37.top");var subQ2=makeQuery(id+"F2.imprint","INTERSECT",VERTEX,{"derivedFrom":[subQ1,subQ0]});Q4=makeQuery(id+"F2.imprint","IMPRINT",FACE,{"disambiguationData":[TD([[makeQuery(id+"F2.imprint","IMPRINT",EDGE,{"disambiguationData":[TD([[subQ2,1.0]])],"derivedFrom":subQ1}),1.0]])]});}
            var Q5;
            {var subQ3=sQuery(id+"F0.wireOp",EDGE,"E12.top");var subQ7=makeQuery(id+"F1.opExtrude","CAP_EDGE",EDGE,{"disambiguationData":[OSD([subQ3])],"isStart":true});Q5=makeQuery(id+"F2.imprint","IMPRINT",FACE,{"disambiguationData":[TD([[makeQuery(id+"F2.imprint","IMPRINT",EDGE,{"derivedFrom":subQ7}),-1.0]])]});}
            var Q6;
            {var subQ15=sQuery(id+"F2.wireOp",EDGE,"E36.bottom");Q6=makeQuery(id+"F2.imprint","IMPRINT",FACE,{"disambiguationData":[TD([[makeQuery(id+"F2.imprint","IMPRINT",EDGE,{"derivedFrom":subQ15}),-1.0]])]});}
            var Q7;
            {var subQ2=makeQuery(id+"F1.opExtrude","CAP_EDGE",EDGE,{"disambiguationData":[OSD([sQuery(id+"F0.wireOp",EDGE,"E15.right")])],"isStart":true});var subQ7=sQuery(id+"F2.wireOp",EDGE,"E46.top");var subQ8=makeQuery(id+"F2.imprint","INTERSECT",VERTEX,{"derivedFrom":[subQ2,subQ7]});Q7=makeQuery(id+"F2.imprint","IMPRINT",FACE,{"disambiguationData":[TD([[makeQuery(id+"F2.imprint","IMPRINT",EDGE,{"disambiguationData":[TD([[subQ8,-1.0]])],"derivedFrom":subQ2}),-1.0]])]});}
            var Q8;
            {var subQ0=sQuery(id+"F2.wireOp",EDGE,"E46.left");Q8=makeQuery(id+"F2.imprint","IMPRINT",FACE,{"disambiguationData":[TD([[makeQuery(id+"F2.imprint","IMPRINT",EDGE,{"derivedFrom":subQ0}),-1.0]])]});}
            var Q9;
            {var subQ0=sQuery(id+"F2.wireOp",EDGE,"E46.right");Q9=makeQuery(id+"F2.imprint","IMPRINT",FACE,{"disambiguationData":[TD([[makeQuery(id+"F2.imprint","IMPRINT",EDGE,{"derivedFrom":subQ0}),1.0]])]});}
            var Q10;
            {var subQ2=makeQuery(id+"F1.opExtrude","CAP_EDGE",EDGE,{"disambiguationData":[OSD([sQuery(id+"F0.wireOp",EDGE,"E14.right")])],"isStart":true});var subQ7=sQuery(id+"F2.wireOp",EDGE,"E47.top");var subQ9=makeQuery(id+"F2.imprint","INTERSECT",VERTEX,{"derivedFrom":[subQ2,subQ7]});Q10=makeQuery(id+"F2.imprint","IMPRINT",FACE,{"disambiguationData":[TD([[makeQuery(id+"F2.imprint","IMPRINT",EDGE,{"disambiguationData":[TD([[subQ9,-1.0]])],"derivedFrom":subQ2}),1.0]])]});}
            var Q11;
            {var subQ0=sQuery(id+"F2.wireOp",EDGE,"E47.right");var subQ7=sQuery(id+"F2.wireOp",EDGE,"E47.top");var subQ8=makeQuery(id+"F2.imprint","INTERSECT",VERTEX,{"derivedFrom":[subQ7,subQ0]});Q11=makeQuery(id+"F2.imprint","IMPRINT",FACE,{"disambiguationData":[TD([[makeQuery(id+"F2.imprint","IMPRINT",EDGE,{"disambiguationData":[TD([[subQ8,1.0]])],"derivedFrom":subQ7}),-1.0]])]});}
            var Q12;
            {var subQ0=sQuery(id+"F2.wireOp",EDGE,"E47.left");Q12=makeQuery(id+"F2.imprint","IMPRINT",FACE,{"disambiguationData":[TD([[makeQuery(id+"F2.imprint","IMPRINT",EDGE,{"derivedFrom":subQ0}),1.0]])]});}
            var Q13;
            {var subQ7=sQuery(id+"F2.wireOp",EDGE,"E39.bottom");var subQ14=sQuery(id+"F0.wireOp",EDGE,"E30.right");var subQ15=makeQuery(id+"F2.imprint","INTERSECT",VERTEX,{"derivedFrom":[makeQuery(id+"F1.opExtrude","CAP_EDGE",EDGE,{"disambiguationData":[OSD([subQ14])],"isStart":true}),subQ7]});Q13=makeQuery(id+"F2.imprint","IMPRINT",FACE,{"disambiguationData":[TD([[makeQuery(id+"F2.imprint","IMPRINT",EDGE,{"disambiguationData":[TD([[subQ15,1.0]])],"derivedFrom":subQ7}),-1.0]])]});}
            var Q14;
            {var subQ0=sQuery(id+"F2.wireOp",EDGE,"E39.right");var subQ1=sQuery(id+"F2.wireOp",EDGE,"E39.top");var subQ2=makeQuery(id+"F2.imprint","INTERSECT",VERTEX,{"derivedFrom":[subQ1,subQ0]});Q14=makeQuery(id+"F2.imprint","IMPRINT",FACE,{"disambiguationData":[TD([[makeQuery(id+"F2.imprint","IMPRINT",EDGE,{"disambiguationData":[TD([[subQ2,1.0]])],"derivedFrom":subQ1}),1.0]])]});}
            var Q15;
            {var subQ0=sQuery(id+"F2.wireOp",EDGE,"E39.left");var subQ1=sQuery(id+"F2.wireOp",EDGE,"E39.top");var subQ2=makeQuery(id+"F2.imprint","INTERSECT",VERTEX,{"derivedFrom":[subQ1,subQ0]});Q15=makeQuery(id+"F2.imprint","IMPRINT",FACE,{"disambiguationData":[TD([[makeQuery(id+"F2.imprint","IMPRINT",EDGE,{"disambiguationData":[TD([[subQ2,-1.0]])],"derivedFrom":subQ1}),1.0]])]});}
            var Q16;
            {var subQ7=sQuery(id+"F2.wireOp",EDGE,"E38.bottom");var subQ22=sQuery(id+"F0.wireOp",EDGE,"E29.right");var subQ23=makeQuery(id+"F2.imprint","INTERSECT",VERTEX,{"derivedFrom":[makeQuery(id+"F1.opExtrude","CAP_EDGE",EDGE,{"disambiguationData":[OSD([subQ22])],"isStart":true}),subQ7]});Q16=makeQuery(id+"F2.imprint","IMPRINT",FACE,{"disambiguationData":[TD([[makeQuery(id+"F2.imprint","IMPRINT",EDGE,{"disambiguationData":[TD([[subQ23,1.0]])],"derivedFrom":subQ7}),-1.0]])]});}
            var Q17;
            {var subQ0=sQuery(id+"F2.wireOp",EDGE,"E38.right");var subQ1=sQuery(id+"F2.wireOp",EDGE,"E38.top");var subQ2=makeQuery(id+"F2.imprint","INTERSECT",VERTEX,{"derivedFrom":[subQ1,subQ0]});Q17=makeQuery(id+"F2.imprint","IMPRINT",FACE,{"disambiguationData":[TD([[makeQuery(id+"F2.imprint","IMPRINT",EDGE,{"disambiguationData":[TD([[subQ2,1.0]])],"derivedFrom":subQ1}),1.0]])]});}
            var Q18;
            {var subQ0=sQuery(id+"F2.wireOp",EDGE,"E38.left");var subQ1=sQuery(id+"F2.wireOp",EDGE,"E38.top");var subQ2=makeQuery(id+"F2.imprint","INTERSECT",VERTEX,{"derivedFrom":[subQ1,subQ0]});Q18=makeQuery(id+"F2.imprint","IMPRINT",FACE,{"disambiguationData":[TD([[makeQuery(id+"F2.imprint","IMPRINT",EDGE,{"disambiguationData":[TD([[subQ2,-1.0]])],"derivedFrom":subQ1}),1.0]])]});}
            var Q19;
            {var subQ7=sQuery(id+"F2.wireOp",EDGE,"E40.bottom");var subQ14=sQuery(id+"F0.wireOp",EDGE,"E28.right");var subQ15=makeQuery(id+"F2.imprint","INTERSECT",VERTEX,{"derivedFrom":[makeQuery(id+"F1.opExtrude","CAP_EDGE",EDGE,{"disambiguationData":[OSD([subQ14])],"isStart":true}),subQ7]});Q19=makeQuery(id+"F2.imprint","IMPRINT",FACE,{"disambiguationData":[TD([[makeQuery(id+"F2.imprint","IMPRINT",EDGE,{"disambiguationData":[TD([[subQ15,1.0]])],"derivedFrom":subQ7}),-1.0]])]});}
            var Q20;
            {var subQ0=sQuery(id+"F2.wireOp",EDGE,"E40.left");var subQ1=sQuery(id+"F2.wireOp",EDGE,"E40.top");var subQ2=makeQuery(id+"F2.imprint","INTERSECT",VERTEX,{"derivedFrom":[subQ1,subQ0]});Q20=makeQuery(id+"F2.imprint","IMPRINT",FACE,{"disambiguationData":[TD([[makeQuery(id+"F2.imprint","IMPRINT",EDGE,{"disambiguationData":[TD([[subQ2,-1.0]])],"derivedFrom":subQ1}),1.0]])]});}
            var Q21;
            {var subQ0=sQuery(id+"F2.wireOp",EDGE,"E40.right");var subQ1=sQuery(id+"F2.wireOp",EDGE,"E40.top");var subQ2=makeQuery(id+"F2.imprint","INTERSECT",VERTEX,{"derivedFrom":[subQ1,subQ0]});Q21=makeQuery(id+"F2.imprint","IMPRINT",FACE,{"disambiguationData":[TD([[makeQuery(id+"F2.imprint","IMPRINT",EDGE,{"disambiguationData":[TD([[subQ2,1.0]])],"derivedFrom":subQ1}),1.0]])]});}
            var Q22;
            {var subQ2=makeQuery(id+"F1.opExtrude","CAP_EDGE",EDGE,{"disambiguationData":[OSD([sQuery(id+"F0.wireOp",EDGE,"E6.right")])],"isStart":true});var subQ7=sQuery(id+"F2.wireOp",EDGE,"E44.top");var subQ8=makeQuery(id+"F2.imprint","INTERSECT",VERTEX,{"derivedFrom":[subQ2,subQ7]});Q22=makeQuery(id+"F2.imprint","IMPRINT",FACE,{"disambiguationData":[TD([[makeQuery(id+"F2.imprint","IMPRINT",EDGE,{"disambiguationData":[TD([[subQ8,-1.0]])],"derivedFrom":subQ2}),-1.0]])]});}
            var Q23;
            {var subQ0=sQuery(id+"F2.wireOp",EDGE,"E44.right");Q23=makeQuery(id+"F2.imprint","IMPRINT",FACE,{"disambiguationData":[TD([[makeQuery(id+"F2.imprint","IMPRINT",EDGE,{"derivedFrom":subQ0}),-1.0]])]});}
            var Q24;
            {var subQ0=sQuery(id+"F2.wireOp",EDGE,"E44.left");Q24=makeQuery(id+"F2.imprint","IMPRINT",FACE,{"disambiguationData":[TD([[makeQuery(id+"F2.imprint","IMPRINT",EDGE,{"derivedFrom":subQ0}),-1.0]])]});}
            var Q25;
            {var subQ2=makeQuery(id+"F1.opExtrude","CAP_EDGE",EDGE,{"disambiguationData":[OSD([sQuery(id+"F0.wireOp",EDGE,"E7.right")])],"isStart":true});var subQ7=sQuery(id+"F2.wireOp",EDGE,"E45.top");var subQ8=makeQuery(id+"F2.imprint","INTERSECT",VERTEX,{"derivedFrom":[subQ2,subQ7]});Q25=makeQuery(id+"F2.imprint","IMPRINT",FACE,{"disambiguationData":[TD([[makeQuery(id+"F2.imprint","IMPRINT",EDGE,{"disambiguationData":[TD([[subQ8,-1.0]])],"derivedFrom":subQ2}),1.0]])]});}
            var Q26;
            {var subQ0=sQuery(id+"F2.wireOp",EDGE,"E45.right");Q26=makeQuery(id+"F2.imprint","IMPRINT",FACE,{"disambiguationData":[TD([[makeQuery(id+"F2.imprint","IMPRINT",EDGE,{"derivedFrom":subQ0}),1.0]])]});}
            var Q27;
            {var subQ0=sQuery(id+"F2.wireOp",EDGE,"E45.left");Q27=makeQuery(id+"F2.imprint","IMPRINT",FACE,{"disambiguationData":[TD([[makeQuery(id+"F2.imprint","IMPRINT",EDGE,{"derivedFrom":subQ0}),1.0]])]});}
            var Q28;
            {var subQ13=sQuery(id+"F2.wireOp",EDGE,"E41.bottom");var subQ23=sQuery(id+"F0.wireOp",EDGE,"E27.right");var subQ24=makeQuery(id+"F2.imprint","INTERSECT",VERTEX,{"derivedFrom":[makeQuery(id+"F1.opExtrude","CAP_EDGE",EDGE,{"disambiguationData":[OSD([subQ23])],"isStart":true}),subQ13]});Q28=makeQuery(id+"F2.imprint","IMPRINT",FACE,{"disambiguationData":[TD([[makeQuery(id+"F2.imprint","IMPRINT",EDGE,{"disambiguationData":[TD([[subQ24,1.0]])],"derivedFrom":subQ13}),-1.0]])]});}
            var Q29;
            {var subQ0=sQuery(id+"F2.wireOp",EDGE,"E41.right");var subQ1=sQuery(id+"F2.wireOp",EDGE,"E41.top");var subQ2=makeQuery(id+"F2.imprint","INTERSECT",VERTEX,{"derivedFrom":[subQ1,subQ0]});Q29=makeQuery(id+"F2.imprint","IMPRINT",FACE,{"disambiguationData":[TD([[makeQuery(id+"F2.imprint","IMPRINT",EDGE,{"disambiguationData":[TD([[subQ2,1.0]])],"derivedFrom":subQ1}),1.0]])]});}
            var Q30;
            {var subQ0=sQuery(id+"F2.wireOp",EDGE,"E41.left");var subQ1=sQuery(id+"F2.wireOp",EDGE,"E41.top");var subQ2=makeQuery(id+"F2.imprint","INTERSECT",VERTEX,{"derivedFrom":[subQ1,subQ0]});Q30=makeQuery(id+"F2.imprint","IMPRINT",FACE,{"disambiguationData":[TD([[makeQuery(id+"F2.imprint","IMPRINT",EDGE,{"disambiguationData":[TD([[subQ2,-1.0]])],"derivedFrom":subQ1}),1.0]])]});}
            var Q31;
            {var subQ7=sQuery(id+"F2.wireOp",EDGE,"E42.bottom");var subQ14=sQuery(id+"F0.wireOp",EDGE,"E26.right");var subQ15=makeQuery(id+"F2.imprint","INTERSECT",VERTEX,{"derivedFrom":[makeQuery(id+"F1.opExtrude","CAP_EDGE",EDGE,{"disambiguationData":[OSD([subQ14])],"isStart":true}),subQ7]});Q31=makeQuery(id+"F2.imprint","IMPRINT",FACE,{"disambiguationData":[TD([[makeQuery(id+"F2.imprint","IMPRINT",EDGE,{"disambiguationData":[TD([[subQ15,1.0]])],"derivedFrom":subQ7}),-1.0]])]});}
            var Q32;
            {var subQ0=sQuery(id+"F2.wireOp",EDGE,"E42.right");var subQ1=sQuery(id+"F2.wireOp",EDGE,"E42.top");var subQ2=makeQuery(id+"F2.imprint","INTERSECT",VERTEX,{"derivedFrom":[subQ1,subQ0]});Q32=makeQuery(id+"F2.imprint","IMPRINT",FACE,{"disambiguationData":[TD([[makeQuery(id+"F2.imprint","IMPRINT",EDGE,{"disambiguationData":[TD([[subQ2,1.0]])],"derivedFrom":subQ1}),1.0]])]});}
            var Q33;
            {var subQ0=sQuery(id+"F2.wireOp",EDGE,"E42.left");var subQ1=sQuery(id+"F2.wireOp",EDGE,"E42.top");var subQ2=makeQuery(id+"F2.imprint","INTERSECT",VERTEX,{"derivedFrom":[subQ1,subQ0]});Q33=makeQuery(id+"F2.imprint","IMPRINT",FACE,{"disambiguationData":[TD([[makeQuery(id+"F2.imprint","IMPRINT",EDGE,{"disambiguationData":[TD([[subQ2,-1.0]])],"derivedFrom":subQ1}),1.0]])]});}
            var Q34;
            {var subQ3=sQuery(id+"F2.wireOp",EDGE,"E43.top");Q34=makeQuery(id+"F2.imprint","IMPRINT",FACE,{"disambiguationData":[TD([[makeQuery(id+"F2.imprint","IMPRINT",EDGE,{"derivedFrom":subQ3}),-1.0]])]});}
            var Q35;
            {var subQ1=sQuery(id+"F0.wireOp",EDGE,"E24.right");var subQ9=makeQuery(id+"F1.opExtrude","CAP_EDGE",EDGE,{"disambiguationData":[OSD([subQ1])],"isStart":true});Q35=makeQuery(id+"F2.imprint","IMPRINT",FACE,{"disambiguationData":[TD([[makeQuery(id+"F2.imprint","IMPRINT",EDGE,{"derivedFrom":subQ9}),-1.0]])]});}
            var Q36;
            {var subQ1=sQuery(id+"F0.wireOp",EDGE,"E24.left");var subQ9=makeQuery(id+"F1.opExtrude","CAP_EDGE",EDGE,{"disambiguationData":[OSD([subQ1])],"isStart":true});Q36=makeQuery(id+"F2.imprint","IMPRINT",FACE,{"disambiguationData":[TD([[makeQuery(id+"F2.imprint","IMPRINT",EDGE,{"derivedFrom":subQ9}),1.0]])]});}
            var Q37;
            {var subQ4=sQuery(id+"F0.wireOp",EDGE,"E4.top");var subQ7=makeQuery(id+"F1.opExtrude","CAP_EDGE",EDGE,{"disambiguationData":[OSD([subQ4])],"isStart":true});Q37=makeQuery(id+"F2.imprint","IMPRINT",FACE,{"disambiguationData":[TD([[makeQuery(id+"F2.imprint","IMPRINT",EDGE,{"derivedFrom":subQ7}),-1.0]])]});}
            var Q38;
            {var subQ12=sQuery(id+"F2.wireOp",EDGE,"E49.bottom");Q38=makeQuery(id+"F2.imprint","IMPRINT",FACE,{"disambiguationData":[TD([[makeQuery(id+"F2.imprint","IMPRINT",EDGE,{"derivedFrom":subQ12}),-1.0]])]});}
            var Q39;
            {var subQ4=sQuery(id+"F0.wireOp",EDGE,"E5.top");var subQ7=makeQuery(id+"F1.opExtrude","CAP_EDGE",EDGE,{"disambiguationData":[OSD([subQ4])],"isStart":true});Q39=makeQuery(id+"F2.imprint","IMPRINT",FACE,{"disambiguationData":[TD([[makeQuery(id+"F2.imprint","IMPRINT",EDGE,{"derivedFrom":subQ7}),1.0]])]});}
            var Q40;
            {var subQ11=sQuery(id+"F2.wireOp",EDGE,"E48.bottom");Q40=makeQuery(id+"F2.imprint","IMPRINT",FACE,{"disambiguationData":[TD([[makeQuery(id+"F2.imprint","IMPRINT",EDGE,{"derivedFrom":subQ11}),-1.0]])]});}
            extrude(context, id + "F3", {"entities" : qUnion([Q0, Q1, Q2, Q3, Q4, Q5, Q6, Q7, Q8, Q9, Q10, Q11, Q12, Q13, Q14, Q15, Q16, Q17, Q18, Q19, Q20, Q21, Q22, Q23, Q24, Q25, Q26, Q27, Q28, Q29, Q30, Q31, Q32, Q33, Q34, Q35, Q36, Q37, Q38, Q39, Q40]), "operationType" : NewBodyOperationType.ADD, "endBound" : BoundingType.SYMMETRIC, "depth" : 101.6 * mm, "offsetDistance" : 25.4 * mm});
        }
        {
            var Q0;
            Q0=makeQuery(id+"F3.boolean.opBoolean","MERGE",FACE,{"derivedFrom":[makeQuery(id+"F1.opExtrude","CAP_FACE",FACE,{"disambiguationData":[OSD([sQuery(id+"F0.wireOp",EDGE,"E0.bottom"),sQuery(id+"F0.wireOp",EDGE,"E0.top"),sQuery(id+"F0.wireOp",EDGE,"E1.top"),sQuery(id+"F0.wireOp",EDGE,"E1.left"),sQuery(id+"F0.wireOp",EDGE,"E1.right"),sQuery(id+"F0.wireOp",EDGE,"E2.top"),sQuery(id+"F0.wireOp",EDGE,"E2.left"),sQuery(id+"F0.wireOp",EDGE,"E2.right"),sQuery(id+"F0.wireOp",EDGE,"E3.bottom"),sQuery(id+"F0.wireOp",EDGE,"E3.top"),sQuery(id+"F0.wireOp",EDGE,"E4.bottom"),sQuery(id+"F0.wireOp",EDGE,"E4.top"),sQuery(id+"F0.wireOp",EDGE,"E4.right"),sQuery(id+"F0.wireOp",EDGE,"E5.bottom"),sQuery(id+"F0.wireOp",EDGE,"E5.top"),sQuery(id+"F0.wireOp",EDGE,"E5.right"),sQuery(id+"F0.wireOp",EDGE,"E6.left"),sQuery(id+"F0.wireOp",EDGE,"E6.right"),sQuery(id+"F0.wireOp",EDGE,"E7.left"),sQuery(id+"F0.wireOp",EDGE,"E7.right"),sQuery(id+"F0.wireOp",EDGE,"E10"),sQuery(id+"F0.wireOp",EDGE,"E11"),sQuery(id+"F0.wireOp",EDGE,"E12.bottom"),sQuery(id+"F0.wireOp",EDGE,"E12.top"),sQuery(id+"F0.wireOp",EDGE,"E12.right"),sQuery(id+"F0.wireOp",EDGE,"E13.bottom"),sQuery(id+"F0.wireOp",EDGE,"E13.top"),sQuery(id+"F0.wireOp",EDGE,"E13.right"),sQuery(id+"F0.wireOp",EDGE,"E14.left"),sQuery(id+"F0.wireOp",EDGE,"E14.right"),sQuery(id+"F0.wireOp",EDGE,"E15.left"),sQuery(id+"F0.wireOp",EDGE,"E15.right"),sQuery(id+"F0.wireOp",EDGE,"E16"),sQuery(id+"F0.wireOp",EDGE,"E17"),sQuery(id+"F0.wireOp",EDGE,"E18.bottom"),sQuery(id+"F0.wireOp",EDGE,"E18.top"),sQuery(id+"F0.wireOp",EDGE,"E19.bottom"),sQuery(id+"F0.wireOp",EDGE,"E19.top"),sQuery(id+"F0.wireOp",EDGE,"E20.bottom"),sQuery(id+"F0.wireOp",EDGE,"E20.top"),sQuery(id+"F0.wireOp",EDGE,"E21.bottom"),sQuery(id+"F0.wireOp",EDGE,"E21.top"),sQuery(id+"F0.wireOp",EDGE,"E22.bottom"),sQuery(id+"F0.wireOp",EDGE,"E22.top"),sQuery(id+"F0.wireOp",EDGE,"E23.bottom"),sQuery(id+"F0.wireOp",EDGE,"E23.top"),sQuery(id+"F0.wireOp",EDGE,"E24.left"),sQuery(id+"F0.wireOp",EDGE,"E24.right"),sQuery(id+"F0.wireOp",EDGE,"E25.left"),sQuery(id+"F0.wireOp",EDGE,"E25.right"),sQuery(id+"F0.wireOp",EDGE,"E26.left"),sQuery(id+"F0.wireOp",EDGE,"E26.right"),sQuery(id+"F0.wireOp",EDGE,"E27.left"),sQuery(id+"F0.wireOp",EDGE,"E27.right"),sQuery(id+"F0.wireOp",EDGE,"E28.left"),sQuery(id+"F0.wireOp",EDGE,"E28.right"),sQuery(id+"F0.wireOp",EDGE,"E29.left"),sQuery(id+"F0.wireOp",EDGE,"E29.right"),sQuery(id+"F0.wireOp",EDGE,"E30.left"),sQuery(id+"F0.wireOp",EDGE,"E30.right"),sQuery(id+"F0.wireOp",EDGE,"E31"),sQuery(id+"F0.wireOp",EDGE,"E32"),sQuery(id+"F0.wireOp",EDGE,"E33"),sQuery(id+"F0.wireOp",EDGE,"E34")])],"isStart":false}),makeQuery(id+"F3.opExtrude","CAP_FACE",FACE,{"disambiguationData":[OSD([sQuery(id+"F2.wireOp",EDGE,"E35.bottom"),sQuery(id+"F2.wireOp",EDGE,"E35.top"),sQuery(id+"F2.wireOp",EDGE,"E35.left"),sQuery(id+"F2.wireOp",EDGE,"E35.right")])],"isStart":true}),makeQuery(id+"F3.opExtrude","CAP_FACE",FACE,{"disambiguationData":[OSD([sQuery(id+"F2.wireOp",EDGE,"E36.bottom"),sQuery(id+"F2.wireOp",EDGE,"E36.top"),sQuery(id+"F2.wireOp",EDGE,"E36.left"),sQuery(id+"F2.wireOp",EDGE,"E36.right")])],"isStart":true}),makeQuery(id+"F3.opExtrude","CAP_FACE",FACE,{"disambiguationData":[OSD([sQuery(id+"F2.wireOp",EDGE,"E37.bottom"),sQuery(id+"F2.wireOp",EDGE,"E37.top"),sQuery(id+"F2.wireOp",EDGE,"E37.left"),sQuery(id+"F2.wireOp",EDGE,"E37.right")])],"isStart":true}),makeQuery(id+"F3.opExtrude","CAP_FACE",FACE,{"disambiguationData":[OSD([sQuery(id+"F2.wireOp",EDGE,"E38.bottom"),sQuery(id+"F2.wireOp",EDGE,"E38.top"),sQuery(id+"F2.wireOp",EDGE,"E38.left"),sQuery(id+"F2.wireOp",EDGE,"E38.right")])],"isStart":true}),makeQuery(id+"F3.opExtrude","CAP_FACE",FACE,{"disambiguationData":[OSD([sQuery(id+"F2.wireOp",EDGE,"E39.bottom"),sQuery(id+"F2.wireOp",EDGE,"E39.top"),sQuery(id+"F2.wireOp",EDGE,"E39.left"),sQuery(id+"F2.wireOp",EDGE,"E39.right")])],"isStart":true}),makeQuery(id+"F3.opExtrude","CAP_FACE",FACE,{"disambiguationData":[OSD([sQuery(id+"F2.wireOp",EDGE,"E40.bottom"),sQuery(id+"F2.wireOp",EDGE,"E40.top"),sQuery(id+"F2.wireOp",EDGE,"E40.left"),sQuery(id+"F2.wireOp",EDGE,"E40.right")])],"isStart":true}),makeQuery(id+"F3.opExtrude","CAP_FACE",FACE,{"disambiguationData":[OSD([sQuery(id+"F2.wireOp",EDGE,"E41.bottom"),sQuery(id+"F2.wireOp",EDGE,"E41.top"),sQuery(id+"F2.wireOp",EDGE,"E41.left"),sQuery(id+"F2.wireOp",EDGE,"E41.right")])],"isStart":true}),makeQuery(id+"F3.opExtrude","CAP_FACE",FACE,{"disambiguationData":[OSD([sQuery(id+"F2.wireOp",EDGE,"E42.bottom"),sQuery(id+"F2.wireOp",EDGE,"E42.top"),sQuery(id+"F2.wireOp",EDGE,"E42.left"),sQuery(id+"F2.wireOp",EDGE,"E42.right")])],"isStart":true}),makeQuery(id+"F3.opExtrude","CAP_FACE",FACE,{"disambiguationData":[OSD([sQuery(id+"F2.wireOp",EDGE,"E43.bottom"),sQuery(id+"F2.wireOp",EDGE,"E43.top"),sQuery(id+"F2.wireOp",EDGE,"E43.left"),sQuery(id+"F2.wireOp",EDGE,"E43.right")])],"isStart":true}),makeQuery(id+"F3.opExtrude","CAP_FACE",FACE,{"disambiguationData":[OSD([sQuery(id+"F2.wireOp",EDGE,"E44.bottom"),sQuery(id+"F2.wireOp",EDGE,"E44.top"),sQuery(id+"F2.wireOp",EDGE,"E44.left"),sQuery(id+"F2.wireOp",EDGE,"E44.right")])],"isStart":true}),makeQuery(id+"F3.opExtrude","CAP_FACE",FACE,{"disambiguationData":[OSD([sQuery(id+"F2.wireOp",EDGE,"E45.bottom"),sQuery(id+"F2.wireOp",EDGE,"E45.top"),sQuery(id+"F2.wireOp",EDGE,"E45.left"),sQuery(id+"F2.wireOp",EDGE,"E45.right")])],"isStart":true}),makeQuery(id+"F3.opExtrude","CAP_FACE",FACE,{"disambiguationData":[OSD([sQuery(id+"F2.wireOp",EDGE,"E46.bottom"),sQuery(id+"F2.wireOp",EDGE,"E46.top"),sQuery(id+"F2.wireOp",EDGE,"E46.left"),sQuery(id+"F2.wireOp",EDGE,"E46.right")])],"isStart":true}),makeQuery(id+"F3.opExtrude","CAP_FACE",FACE,{"disambiguationData":[OSD([sQuery(id+"F2.wireOp",EDGE,"E47.bottom"),sQuery(id+"F2.wireOp",EDGE,"E47.top"),sQuery(id+"F2.wireOp",EDGE,"E47.left"),sQuery(id+"F2.wireOp",EDGE,"E47.right")])],"isStart":true}),makeQuery(id+"F3.opExtrude","CAP_FACE",FACE,{"disambiguationData":[OSD([sQuery(id+"F2.wireOp",EDGE,"E48.bottom"),sQuery(id+"F2.wireOp",EDGE,"E48.top"),sQuery(id+"F2.wireOp",EDGE,"E48.left"),sQuery(id+"F2.wireOp",EDGE,"E48.right")])],"isStart":true}),makeQuery(id+"F3.opExtrude","CAP_FACE",FACE,{"disambiguationData":[OSD([sQuery(id+"F2.wireOp",EDGE,"E49.bottom"),sQuery(id+"F2.wireOp",EDGE,"E49.top"),sQuery(id+"F2.wireOp",EDGE,"E49.left"),sQuery(id+"F2.wireOp",EDGE,"E49.right")])],"isStart":true})]});
            var sketch = newSketch(context, id + "F4", { "sketchPlane" : qUnion([Q0])});
            skLineSegment(sketch, "E50.bottom", {"start": v(-750.69, 249) * mm, "end": v(265.31, 249) * mm});
            skLineSegment(sketch, "E50.top", {"start": v(-750.69, 198.2) * mm, "end": v(265.31, 198.2) * mm});
            skLineSegment(sketch, "E50.left", {"start": v(-750.69, 249) * mm, "end": v(-750.69, 198.2) * mm});
            skLineSegment(sketch, "E50.right", {"start": v(265.31, 249) * mm, "end": v(265.31, 198.2) * mm});
            skSolve(sketch);
        }
        {
            var Q0;
            Q0=makeQuery(id+"F4.imprint","IMPRINT",FACE,{"disambiguationData":[TD([[makeQuery(id+"F4.imprint","IMPRINT",EDGE,{"derivedFrom":sQuery(id+"F4.wireOp",EDGE,"E50.bottom")}),-1.0]])]});
            extrude(context, id + "F5", {"entities" : qUnion([Q0]), "operationType" : NewBodyOperationType.ADD, "oppositeDirection" : true, "depth" : 50.8 * mm, "offsetDistance" : 25.4 * mm});
        }
        {
            var Q0;
            Q0=makeQuery(id+"F5.boolean.opBoolean","MERGE",FACE,{"derivedFrom":[makeQuery(id+"F3.boolean.opBoolean","MERGE",FACE,{"derivedFrom":[makeQuery(id+"F1.opExtrude","CAP_FACE",FACE,{"disambiguationData":[OSD([sQuery(id+"F0.wireOp",EDGE,"E0.bottom"),sQuery(id+"F0.wireOp",EDGE,"E0.top"),sQuery(id+"F0.wireOp",EDGE,"E1.top"),sQuery(id+"F0.wireOp",EDGE,"E1.left"),sQuery(id+"F0.wireOp",EDGE,"E1.right"),sQuery(id+"F0.wireOp",EDGE,"E2.top"),sQuery(id+"F0.wireOp",EDGE,"E2.left"),sQuery(id+"F0.wireOp",EDGE,"E2.right"),sQuery(id+"F0.wireOp",EDGE,"E3.bottom"),sQuery(id+"F0.wireOp",EDGE,"E3.top"),sQuery(id+"F0.wireOp",EDGE,"E4.bottom"),sQuery(id+"F0.wireOp",EDGE,"E4.top"),sQuery(id+"F0.wireOp",EDGE,"E4.right"),sQuery(id+"F0.wireOp",EDGE,"E5.bottom"),sQuery(id+"F0.wireOp",EDGE,"E5.top"),sQuery(id+"F0.wireOp",EDGE,"E5.right"),sQuery(id+"F0.wireOp",EDGE,"E6.left"),sQuery(id+"F0.wireOp",EDGE,"E6.right"),sQuery(id+"F0.wireOp",EDGE,"E7.left"),sQuery(id+"F0.wireOp",EDGE,"E7.right"),sQuery(id+"F0.wireOp",EDGE,"E10"),sQuery(id+"F0.wireOp",EDGE,"E11"),sQuery(id+"F0.wireOp",EDGE,"E12.bottom"),sQuery(id+"F0.wireOp",EDGE,"E12.top"),sQuery(id+"F0.wireOp",EDGE,"E12.right"),sQuery(id+"F0.wireOp",EDGE,"E13.bottom"),sQuery(id+"F0.wireOp",EDGE,"E13.top"),sQuery(id+"F0.wireOp",EDGE,"E13.right"),sQuery(id+"F0.wireOp",EDGE,"E14.left"),sQuery(id+"F0.wireOp",EDGE,"E14.right"),sQuery(id+"F0.wireOp",EDGE,"E15.left"),sQuery(id+"F0.wireOp",EDGE,"E15.right"),sQuery(id+"F0.wireOp",EDGE,"E16"),sQuery(id+"F0.wireOp",EDGE,"E17"),sQuery(id+"F0.wireOp",EDGE,"E18.bottom"),sQuery(id+"F0.wireOp",EDGE,"E18.top"),sQuery(id+"F0.wireOp",EDGE,"E19.bottom"),sQuery(id+"F0.wireOp",EDGE,"E19.top"),sQuery(id+"F0.wireOp",EDGE,"E20.bottom"),sQuery(id+"F0.wireOp",EDGE,"E20.top"),sQuery(id+"F0.wireOp",EDGE,"E21.bottom"),sQuery(id+"F0.wireOp",EDGE,"E21.top"),sQuery(id+"F0.wireOp",EDGE,"E22.bottom"),sQuery(id+"F0.wireOp",EDGE,"E22.top"),sQuery(id+"F0.wireOp",EDGE,"E23.bottom"),sQuery(id+"F0.wireOp",EDGE,"E23.top"),sQuery(id+"F0.wireOp",EDGE,"E24.left"),sQuery(id+"F0.wireOp",EDGE,"E24.right"),sQuery(id+"F0.wireOp",EDGE,"E25.left"),sQuery(id+"F0.wireOp",EDGE,"E25.right"),sQuery(id+"F0.wireOp",EDGE,"E26.left"),sQuery(id+"F0.wireOp",EDGE,"E26.right"),sQuery(id+"F0.wireOp",EDGE,"E27.left"),sQuery(id+"F0.wireOp",EDGE,"E27.right"),sQuery(id+"F0.wireOp",EDGE,"E28.left"),sQuery(id+"F0.wireOp",EDGE,"E28.right"),sQuery(id+"F0.wireOp",EDGE,"E29.left"),sQuery(id+"F0.wireOp",EDGE,"E29.right"),sQuery(id+"F0.wireOp",EDGE,"E30.left"),sQuery(id+"F0.wireOp",EDGE,"E30.right"),sQuery(id+"F0.wireOp",EDGE,"E31"),sQuery(id+"F0.wireOp",EDGE,"E32"),sQuery(id+"F0.wireOp",EDGE,"E33"),sQuery(id+"F0.wireOp",EDGE,"E34")])],"isStart":false}),makeQuery(id+"F3.opExtrude","CAP_FACE",FACE,{"disambiguationData":[OSD([sQuery(id+"F2.wireOp",EDGE,"E35.bottom"),sQuery(id+"F2.wireOp",EDGE,"E35.top"),sQuery(id+"F2.wireOp",EDGE,"E35.left"),sQuery(id+"F2.wireOp",EDGE,"E35.right")])],"isStart":true}),makeQuery(id+"F3.opExtrude","CAP_FACE",FACE,{"disambiguationData":[OSD([sQuery(id+"F2.wireOp",EDGE,"E36.bottom"),sQuery(id+"F2.wireOp",EDGE,"E36.top"),sQuery(id+"F2.wireOp",EDGE,"E36.left"),sQuery(id+"F2.wireOp",EDGE,"E36.right")])],"isStart":true}),makeQuery(id+"F3.opExtrude","CAP_FACE",FACE,{"disambiguationData":[OSD([sQuery(id+"F2.wireOp",EDGE,"E37.bottom"),sQuery(id+"F2.wireOp",EDGE,"E37.top"),sQuery(id+"F2.wireOp",EDGE,"E37.left"),sQuery(id+"F2.wireOp",EDGE,"E37.right")])],"isStart":true}),makeQuery(id+"F3.opExtrude","CAP_FACE",FACE,{"disambiguationData":[OSD([sQuery(id+"F2.wireOp",EDGE,"E38.bottom"),sQuery(id+"F2.wireOp",EDGE,"E38.top"),sQuery(id+"F2.wireOp",EDGE,"E38.left"),sQuery(id+"F2.wireOp",EDGE,"E38.right")])],"isStart":true}),makeQuery(id+"F3.opExtrude","CAP_FACE",FACE,{"disambiguationData":[OSD([sQuery(id+"F2.wireOp",EDGE,"E39.bottom"),sQuery(id+"F2.wireOp",EDGE,"E39.top"),sQuery(id+"F2.wireOp",EDGE,"E39.left"),sQuery(id+"F2.wireOp",EDGE,"E39.right")])],"isStart":true}),makeQuery(id+"F3.opExtrude","CAP_FACE",FACE,{"disambiguationData":[OSD([sQuery(id+"F2.wireOp",EDGE,"E40.bottom"),sQuery(id+"F2.wireOp",EDGE,"E40.top"),sQuery(id+"F2.wireOp",EDGE,"E40.left"),sQuery(id+"F2.wireOp",EDGE,"E40.right")])],"isStart":true}),makeQuery(id+"F3.opExtrude","CAP_FACE",FACE,{"disambiguationData":[OSD([sQuery(id+"F2.wireOp",EDGE,"E41.bottom"),sQuery(id+"F2.wireOp",EDGE,"E41.top"),sQuery(id+"F2.wireOp",EDGE,"E41.left"),sQuery(id+"F2.wireOp",EDGE,"E41.right")])],"isStart":true}),makeQuery(id+"F3.opExtrude","CAP_FACE",FACE,{"disambiguationData":[OSD([sQuery(id+"F2.wireOp",EDGE,"E42.bottom"),sQuery(id+"F2.wireOp",EDGE,"E42.top"),sQuery(id+"F2.wireOp",EDGE,"E42.left"),sQuery(id+"F2.wireOp",EDGE,"E42.right")])],"isStart":true}),makeQuery(id+"F3.opExtrude","CAP_FACE",FACE,{"disambiguationData":[OSD([sQuery(id+"F2.wireOp",EDGE,"E43.bottom"),sQuery(id+"F2.wireOp",EDGE,"E43.top"),sQuery(id+"F2.wireOp",EDGE,"E43.left"),sQuery(id+"F2.wireOp",EDGE,"E43.right")])],"isStart":true}),makeQuery(id+"F3.opExtrude","CAP_FACE",FACE,{"disambiguationData":[OSD([sQuery(id+"F2.wireOp",EDGE,"E44.bottom"),sQuery(id+"F2.wireOp",EDGE,"E44.top"),sQuery(id+"F2.wireOp",EDGE,"E44.left"),sQuery(id+"F2.wireOp",EDGE,"E44.right")])],"isStart":true}),makeQuery(id+"F3.opExtrude","CAP_FACE",FACE,{"disambiguationData":[OSD([sQuery(id+"F2.wireOp",EDGE,"E45.bottom"),sQuery(id+"F2.wireOp",EDGE,"E45.top"),sQuery(id+"F2.wireOp",EDGE,"E45.left"),sQuery(id+"F2.wireOp",EDGE,"E45.right")])],"isStart":true}),makeQuery(id+"F3.opExtrude","CAP_FACE",FACE,{"disambiguationData":[OSD([sQuery(id+"F2.wireOp",EDGE,"E46.bottom"),sQuery(id+"F2.wireOp",EDGE,"E46.top"),sQuery(id+"F2.wireOp",EDGE,"E46.left"),sQuery(id+"F2.wireOp",EDGE,"E46.right")])],"isStart":true}),makeQuery(id+"F3.opExtrude","CAP_FACE",FACE,{"disambiguationData":[OSD([sQuery(id+"F2.wireOp",EDGE,"E47.bottom"),sQuery(id+"F2.wireOp",EDGE,"E47.top"),sQuery(id+"F2.wireOp",EDGE,"E47.left"),sQuery(id+"F2.wireOp",EDGE,"E47.right")])],"isStart":true}),makeQuery(id+"F3.opExtrude","CAP_FACE",FACE,{"disambiguationData":[OSD([sQuery(id+"F2.wireOp",EDGE,"E48.bottom"),sQuery(id+"F2.wireOp",EDGE,"E48.top"),sQuery(id+"F2.wireOp",EDGE,"E48.left"),sQuery(id+"F2.wireOp",EDGE,"E48.right")])],"isStart":true}),makeQuery(id+"F3.opExtrude","CAP_FACE",FACE,{"disambiguationData":[OSD([sQuery(id+"F2.wireOp",EDGE,"E49.bottom"),sQuery(id+"F2.wireOp",EDGE,"E49.top"),sQuery(id+"F2.wireOp",EDGE,"E49.left"),sQuery(id+"F2.wireOp",EDGE,"E49.right")])],"isStart":true})]}),makeQuery(id+"F5.opExtrude","CAP_FACE",FACE,{"disambiguationData":[OSD([sQuery(id+"F4.wireOp",EDGE,"E50.bottom"),sQuery(id+"F4.wireOp",EDGE,"E50.top"),sQuery(id+"F4.wireOp",EDGE,"E50.left"),sQuery(id+"F4.wireOp",EDGE,"E50.right")])],"isStart":true})]});
            var sketch = newSketch(context, id + "F6", { "sketchPlane" : qUnion([Q0])});
            skLineSegment(sketch, "E51.bottom", {"start": v(-693.54, 204.54) * mm, "end": v(208.16, 204.54) * mm});
            skLineSegment(sketch, "E51.top", {"start": v(-693.54, 2604.84) * mm, "end": v(208.16, 2604.84) * mm});
            skLineSegment(sketch, "E51.left", {"start": v(-693.54, 204.54) * mm, "end": v(-693.54, 2604.84) * mm});
            skLineSegment(sketch, "E51.right", {"start": v(208.16, 204.54) * mm, "end": v(208.16, 2604.84) * mm});
            skSolve(sketch);
        }
        {
            var Q0;
            Q0 = qSketchRegion(id + "F6", true);
            extrude(context, id + "F7", {"entities" : qUnion([Q0]), "depth" : 1400.05 * mm, "offsetDistance" : 25.4 * mm});
        }
    });
